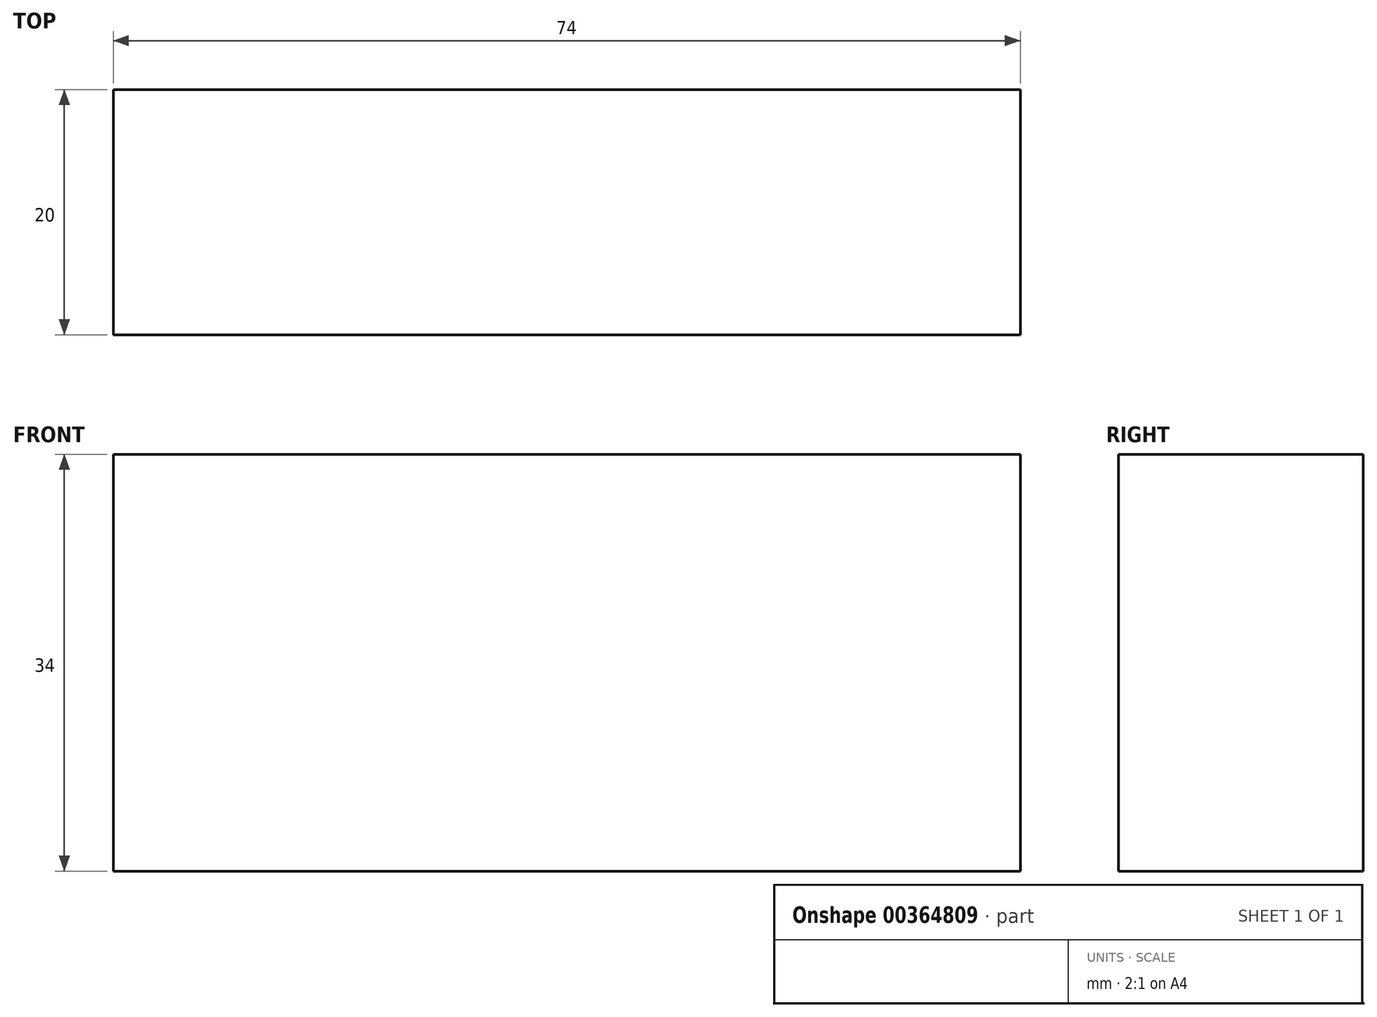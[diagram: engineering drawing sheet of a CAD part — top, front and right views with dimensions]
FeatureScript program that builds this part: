
annotation { "Feature Type Name" : "Feature", "Feature Type Description" : "" }
export const myFeature = defineFeature(function(context is Context, id is Id, definition is map)
    precondition{}
    {
        {
            var Q0;
            Q0=qCreatedBy(makeId("Front.planeOp"),FACE);
            var sketch = newSketch(context, id + "F0", { "sketchPlane" : qUnion([Q0])});
            skLineSegment(sketch, "E0.bottom", {"start": v(37, -17) * mm, "end": v(-37, -17) * mm});
            skLineSegment(sketch, "E0.top", {"start": v(37, 17) * mm, "end": v(-37, 17) * mm});
            skLineSegment(sketch, "E0.left", {"start": v(37, -17) * mm, "end": v(37, 17) * mm});
            skLineSegment(sketch, "E0.right", {"start": v(-37, -17) * mm, "end": v(-37, 17) * mm});
            skPoint(sketch, "E0.middle", {"position": v(0, 0) * mm});
            skSolve(sketch);
        }
        {
            var Q0;
            Q0=makeQuery(id+"F0.imprint","IMPRINT",FACE,{"disambiguationData":[TD([[makeQuery(id+"F0.imprint","IMPRINT",EDGE,{"derivedFrom":sQuery(id+"F0.wireOp",EDGE,"E0.bottom")}),-1.0]])]});
            extrude(context, id + "F1", {"entities" : qUnion([Q0]), "depth" : 20 * mm});
        }
    });
